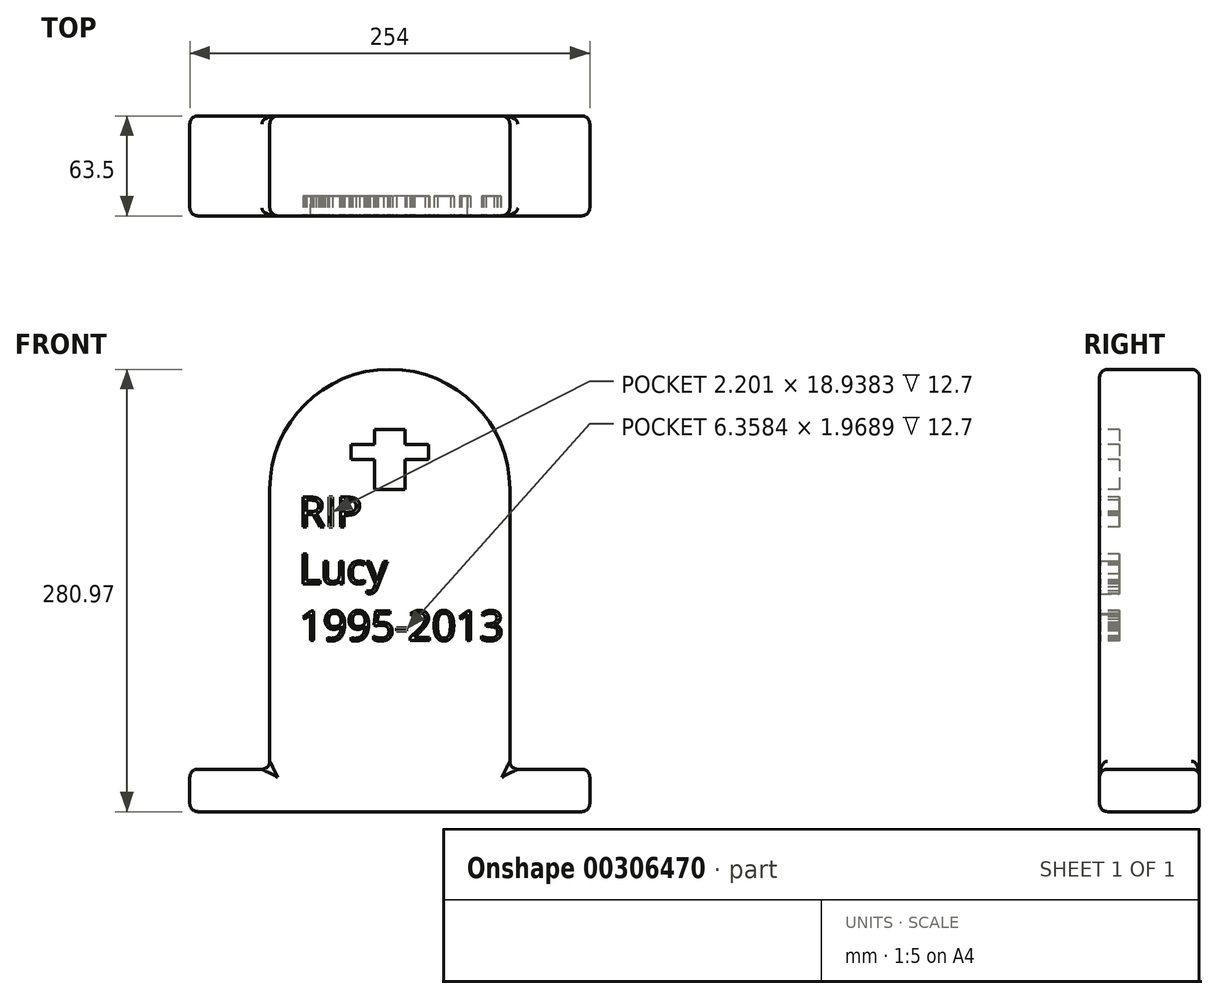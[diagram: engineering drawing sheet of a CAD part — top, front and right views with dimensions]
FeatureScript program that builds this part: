
annotation { "Feature Type Name" : "Feature", "Feature Type Description" : "" }
export const myFeature = defineFeature(function(context is Context, id is Id, definition is map)
    precondition{}
    {
        {
            var Q0;
            Q0=qCreatedBy(makeId("Front.planeOp"),FACE);
            var sketch = newSketch(context, id + "F0", { "sketchPlane" : qUnion([Q0])});
            skLineSegment(sketch, "E0.bottom", {"start": v(-76.63, 122.15) * mm, "end": v(75.77, 122.15) * mm});
            skLineSegment(sketch, "E0.top", {"start": v(-76.63, -55.65) * mm, "end": v(75.77, -55.65) * mm});
            skLineSegment(sketch, "E0.left", {"start": v(-76.63, 122.15) * mm, "end": v(-76.63, -55.65) * mm});
            skLineSegment(sketch, "E0.right", {"start": v(75.77, 122.15) * mm, "end": v(75.77, -55.65) * mm});
            skArc(sketch, "E1", {"start": v(75.77, 122.15) * mm, "mid": v(-0.43, 198.35) * mm, "end": v(-76.63, 122.15) * mm});
            skLineSegment(sketch, "E2.bottom", {"start": v(-0.43, -55.65) * mm, "end": v(-127.43, -55.65) * mm});
            skLineSegment(sketch, "E2.top", {"start": v(-0.43, -82.62) * mm, "end": v(-127.43, -82.62) * mm});
            skLineSegment(sketch, "E2.left", {"start": v(-0.43, -55.65) * mm, "end": v(-0.43, -82.62) * mm});
            skLineSegment(sketch, "E2.right", {"start": v(-127.43, -55.65) * mm, "end": v(-127.43, -82.62) * mm});
            skLineSegment(sketch, "E3.MirrorCS", {"start": v(-0.43, -82.62) * mm, "end": v(126.57, -82.62) * mm});
            skLineSegment(sketch, "E4.MirrorCS", {"start": v(-0.43, -55.65) * mm, "end": v(126.57, -55.65) * mm});
            skLineSegment(sketch, "E5.MirrorCS", {"start": v(126.57, -55.65) * mm, "end": v(126.57, -82.62) * mm});
            skSolve(sketch);
        }
        {
            var Q0;
            Q0=makeQuery(id+"F0.imprint","IMPRINT",FACE,{"disambiguationData":[TD([[makeQuery(id+"F0.imprint","IMPRINT",EDGE,{"derivedFrom":sQuery(id+"F0.wireOp",EDGE,"E0.bottom")}),1.0]])]});
            var Q1;
            Q1=makeQuery(id+"F0.imprint","IMPRINT",FACE,{"disambiguationData":[TD([[makeQuery(id+"F0.imprint","IMPRINT",EDGE,{"derivedFrom":sQuery(id+"F0.wireOp",EDGE,"E0.bottom")}),-1.0]])]});
            var Q2;
            {var subQ3=sQuery(id+"F0.wireOp",EDGE,"E2.left");Q2=makeQuery(id+"F0.imprint","IMPRINT",FACE,{"disambiguationData":[TD([[makeQuery(id+"F0.imprint","IMPRINT",EDGE,{"derivedFrom":subQ3}),1.0]])]});}
            var Q3;
            Q3=makeQuery(id+"F0.imprint","IMPRINT",FACE,{"disambiguationData":[TD([[makeQuery(id+"F0.imprint","IMPRINT",EDGE,{"derivedFrom":sQuery(id+"F0.wireOp",EDGE,"E2.top")}),-1.0]])]});
            extrude(context, id + "F1", {"entities" : qUnion([Q0, Q1, Q2, Q3]), "depth" : 63.5 * mm});
        }
        {
            var Q0;
            Q0=makeQuery(id+"F1.opExtrude","CAP_FACE",FACE,{"disambiguationData":[OSD([sQuery(id+"F0.wireOp",EDGE,"E0.left"),sQuery(id+"F0.wireOp",EDGE,"E0.right"),sQuery(id+"F0.wireOp",EDGE,"E1"),sQuery(id+"F0.wireOp",EDGE,"E2.bottom"),sQuery(id+"F0.wireOp",EDGE,"E2.top"),sQuery(id+"F0.wireOp",EDGE,"E2.right"),sQuery(id+"F0.wireOp",EDGE,"E3.MirrorCS"),sQuery(id+"F0.wireOp",EDGE,"E4.MirrorCS"),sQuery(id+"F0.wireOp",EDGE,"E5.MirrorCS")])],"isStart":false});
            var sketch = newSketch(context, id + "F2", { "sketchPlane" : qUnion([Q0])});
            skText(sketch, "E6", { "text": "RIP\nLucy\n1995-2013", "fontName": "OpenSans-Regular.ttf"});
            const initialGuessF2  = {"E6": [-0.058, 0.0982, 1, 0, 0.0191]};
            skSetInitialGuess(sketch, initialGuessF2);
            skSolve(sketch);
        }
        {
            var Q0;
            Q0 = qSketchRegion(id + "F2", true);
            extrude(context, id + "F3", {"entities" : qUnion([Q0]), "operationType" : NewBodyOperationType.REMOVE, "oppositeDirection" : true, "depth" : 12.7 * mm});
        }
        {
            var Q0;
            {var subQ0=sQuery(id+"F0.wireOp",EDGE,"E1");var subQ1=sQuery(id+"F0.wireOp",EDGE,"E5.MirrorCS");var subQ2=sQuery(id+"F0.wireOp",EDGE,"E4.MirrorCS");var subQ3=sQuery(id+"F0.wireOp",EDGE,"E2.right");var subQ4=sQuery(id+"F0.wireOp",EDGE,"E3.MirrorCS");var subQ5=sQuery(id+"F0.wireOp",EDGE,"E2.top");var subQ6=sQuery(id+"F0.wireOp",EDGE,"E0.left");var subQ7=sQuery(id+"F0.wireOp",EDGE,"E2.bottom");var subQ8=sQuery(id+"F0.wireOp",EDGE,"E0.right");Q0=makeQuery(id+"F3.boolean.opBoolean","SPLIT",FACE,{"disambiguationData":[TD([makeQuery(id+"F1.opExtrude","SWEPT_FACE",FACE,{"disambiguationData":[OSD([subQ6])]})])],"derivedFrom":makeQuery(id+"F1.opExtrude","CAP_FACE",FACE,{"disambiguationData":[OSD([subQ6,subQ8,subQ0,subQ7,subQ5,subQ3,subQ4,subQ2,subQ1])],"isStart":false})});}
            var sketch = newSketch(context, id + "F4", { "sketchPlane" : qUnion([Q0])});
            skLineSegment(sketch, "E7", {"start": v(-0.43, 122.15) * mm, "end": v(-0.43, 198.35) * mm, "construction": true});
            skLineSegment(sketch, "E8", {"start": v(-0.43, 160.25) * mm, "end": v(-10.25, 160.25) * mm});
            skLineSegment(sketch, "E9", {"start": v(-10.25, 160.25) * mm, "end": v(-10.25, 150.72) * mm});
            skLineSegment(sketch, "E10", {"start": v(-10.25, 150.72) * mm, "end": v(-25.1, 150.72) * mm});
            skLineSegment(sketch, "E11", {"start": v(-25.1, 150.72) * mm, "end": v(-25.1, 141.17) * mm});
            skLineSegment(sketch, "E12", {"start": v(-25.1, 141.17) * mm, "end": v(-10.25, 141.17) * mm});
            skLineSegment(sketch, "E13", {"start": v(-10.25, 141.17) * mm, "end": v(-10.25, 122.15) * mm});
            skLineSegment(sketch, "E14", {"start": v(-10.25, 122.15) * mm, "end": v(-0.43, 122.15) * mm});
            skLineSegment(sketch, "E15.MirrorCS", {"start": v(-0.43, 160.25) * mm, "end": v(9.38, 160.25) * mm});
            skLineSegment(sketch, "E16.MirrorCS", {"start": v(9.38, 150.72) * mm, "end": v(24.24, 150.72) * mm});
            skLineSegment(sketch, "E17.MirrorCS", {"start": v(9.38, 160.25) * mm, "end": v(9.38, 150.72) * mm});
            skLineSegment(sketch, "E18.MirrorCS", {"start": v(24.24, 141.17) * mm, "end": v(9.38, 141.17) * mm});
            skLineSegment(sketch, "E19.MirrorCS", {"start": v(9.38, 141.17) * mm, "end": v(9.38, 122.15) * mm});
            skLineSegment(sketch, "E20.MirrorCS", {"start": v(9.38, 122.15) * mm, "end": v(-0.43, 122.15) * mm});
            skLineSegment(sketch, "E21.MirrorCS", {"start": v(24.24, 150.72) * mm, "end": v(24.24, 141.17) * mm});
            skSolve(sketch);
        }
        {
            var Q0;
            Q0 = qSketchRegion(id + "F4", true);
            extrude(context, id + "F5", {"entities" : qUnion([Q0]), "operationType" : NewBodyOperationType.REMOVE, "oppositeDirection" : true, "depth" : 12.7 * mm});
        }
        {
            var Q0;
            Q0=makeQuery(id+"F1.opExtrude","CAP_EDGE",EDGE,{"disambiguationData":[OSD([sQuery(id+"F0.wireOp",EDGE,"E2.bottom")])],"isStart":false});
            var Q1;
            Q1=makeQuery(id+"F1.opExtrude","CAP_EDGE",EDGE,{"disambiguationData":[OSD([sQuery(id+"F0.wireOp",EDGE,"E0.left")])],"isStart":false});
            var Q2;
            Q2=makeQuery(id+"F1.opExtrude","CAP_EDGE",EDGE,{"disambiguationData":[OSD([sQuery(id+"F0.wireOp",EDGE,"E4.MirrorCS")])],"isStart":false});
            var Q3;
            Q3=makeQuery(id+"F1.opExtrude","CAP_EDGE",EDGE,{"disambiguationData":[OSD([sQuery(id+"F0.wireOp",EDGE,"E5.MirrorCS")])],"isStart":false});
            var Q4;
            Q4=makeQuery(id+"F1.opExtrude","CAP_EDGE",EDGE,{"disambiguationData":[OSD([sQuery(id+"F0.wireOp",EDGE,"E2.top"),sQuery(id+"F0.wireOp",EDGE,"E3.MirrorCS")])],"isStart":false});
            var Q5;
            Q5=makeQuery(id+"F1.opExtrude","CAP_EDGE",EDGE,{"disambiguationData":[OSD([sQuery(id+"F0.wireOp",EDGE,"E2.right")])],"isStart":false});
            fillet(context, id + "F6", {"entities" : qUnion([Q0, Q1, Q2, Q3, Q4, Q5]), "radius" : 5.08 * mm, "tangentPropagation" : true, "allowEdgeOverflow" : false});
        }
        {
            var Q0;
            Q0=makeQuery(id+"F1.opExtrude","CAP_EDGE",EDGE,{"disambiguationData":[OSD([sQuery(id+"F0.wireOp",EDGE,"E1")])],"isStart":true});
            var Q1;
            Q1=makeQuery(id+"F1.opExtrude","CAP_EDGE",EDGE,{"disambiguationData":[OSD([sQuery(id+"F0.wireOp",EDGE,"E4.MirrorCS")])],"isStart":true});
            var Q2;
            Q2=makeQuery(id+"F1.opExtrude","SWEPT_FACE",FACE,{"disambiguationData":[OSD([sQuery(id+"F0.wireOp",EDGE,"E5.MirrorCS")])]});
            var Q3;
            Q3=makeQuery(id+"F1.opExtrude","SWEPT_EDGE",EDGE,{"disambiguationData":[OSD([sQuery(id+"F0.wireOp",EDGE,"E2.bottom"),sQuery(id+"F0.wireOp",EDGE,"E2.right")])]});
            var Q4;
            Q4=makeQuery(id+"F1.opExtrude","CAP_EDGE",EDGE,{"disambiguationData":[OSD([sQuery(id+"F0.wireOp",EDGE,"E2.bottom")])],"isStart":true});
            var Q5;
            Q5=makeQuery(id+"F1.opExtrude","SWEPT_FACE",FACE,{"disambiguationData":[OSD([sQuery(id+"F0.wireOp",EDGE,"E2.right")])]});
            var Q6;
            Q6=makeQuery(id+"F1.opExtrude","CAP_EDGE",EDGE,{"disambiguationData":[OSD([sQuery(id+"F0.wireOp",EDGE,"E2.top"),sQuery(id+"F0.wireOp",EDGE,"E3.MirrorCS")])],"isStart":true});
            fillet(context, id + "F7", {"entities" : qUnion([Q0, Q1, Q2, Q3, Q4, Q5, Q6]), "radius" : 5.08 * mm, "tangentPropagation" : true, "allowEdgeOverflow" : false});
        }
        {
            var Q0;
            Q0=makeQuery(id+"F1.opExtrude","SWEPT_EDGE",EDGE,{"disambiguationData":[OSD([sQuery(id+"F0.wireOp",EDGE,"E0.left"),sQuery(id+"F0.wireOp",EDGE,"E2.bottom")])]});
            var Q1;
            Q1=makeQuery(id+"F1.opExtrude","SWEPT_EDGE",EDGE,{"disambiguationData":[OSD([sQuery(id+"F0.wireOp",EDGE,"E0.right"),sQuery(id+"F0.wireOp",EDGE,"E4.MirrorCS")])]});
            fillet(context, id + "F8", {"entities" : qUnion([Q0, Q1]), "radius" : 5.08 * mm, "tangentPropagation" : true, "allowEdgeOverflow" : false});
        }
    });
